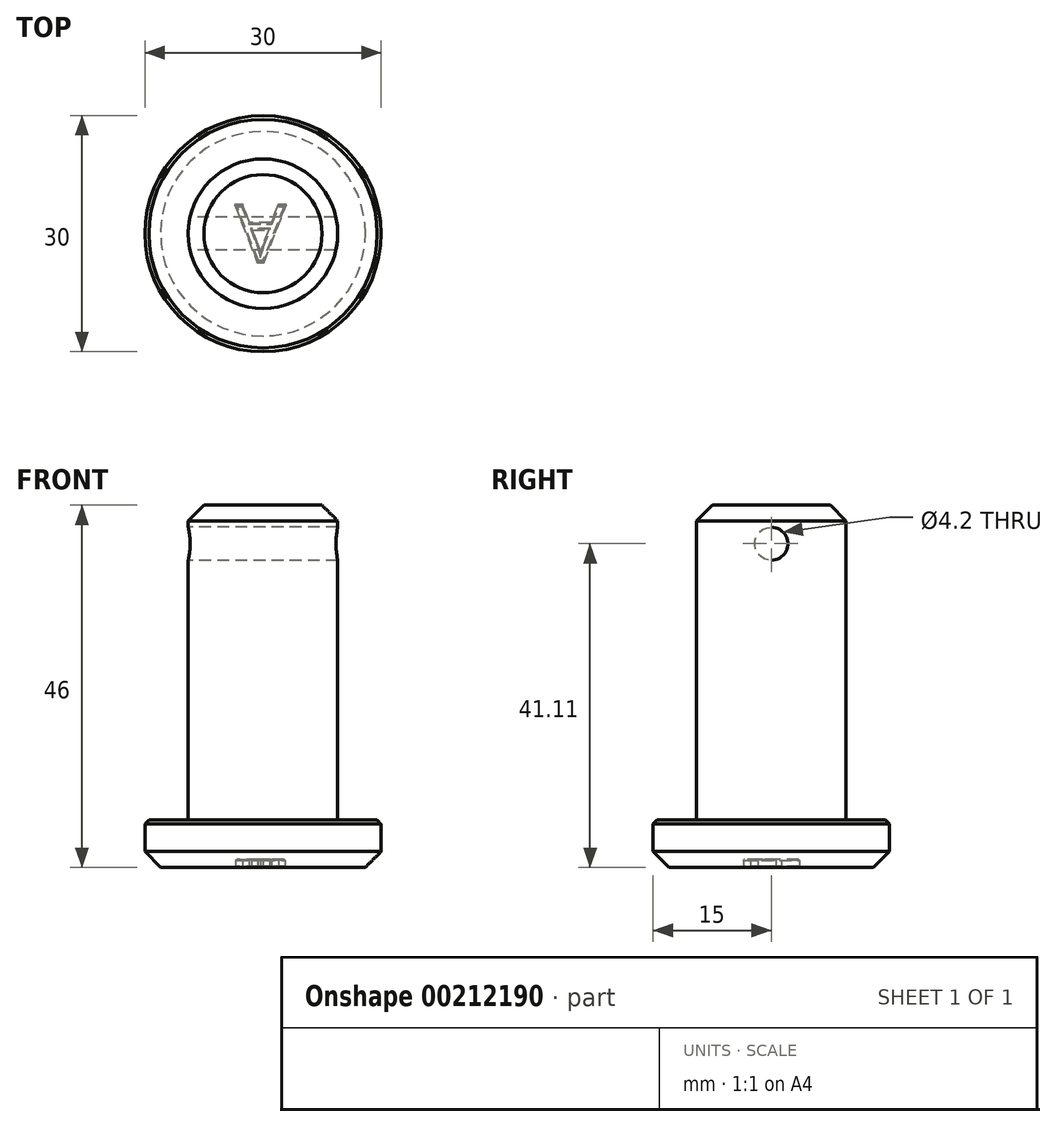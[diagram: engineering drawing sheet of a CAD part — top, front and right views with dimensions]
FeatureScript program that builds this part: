
annotation { "Feature Type Name" : "Feature", "Feature Type Description" : "" }
export const myFeature = defineFeature(function(context is Context, id is Id, definition is map)
    precondition{}
    {
        {
            var Q0;
            Q0=qCreatedBy(makeId("Top.planeOp"),FACE);
            var sketch = newSketch(context, id + "F0", { "sketchPlane" : qUnion([Q0])});
            skCircle(sketch, "E0", {"center": v(0, 0) * mm, "radius": 15 * mm});
            skCircle(sketch, "E1", {"center": v(0, 0) * mm, "radius": 9.5 * mm});
            skSolve(sketch);
        }
        {
            var Q0;
            Q0=makeQuery(id+"F0.imprint","IMPRINT",FACE,{"disambiguationData":[TD([[makeQuery(id+"F0.imprint","IMPRINT",EDGE,{"derivedFrom":sQuery(id+"F0.wireOp",EDGE,"E0")}),1.0]])]});
            extrude(context, id + "F1", {"entities" : qUnion([Q0]), "depth" : 6 * mm});
        }
        {
            var Q0;
            Q0=makeQuery(id+"F0.imprint","IMPRINT",FACE,{"disambiguationData":[TD([[makeQuery(id+"F0.imprint","IMPRINT",EDGE,{"derivedFrom":sQuery(id+"F0.wireOp",EDGE,"E1")}),1.0]])]});
            extrude(context, id + "F2", {"entities" : qUnion([Q0]), "operationType" : NewBodyOperationType.ADD, "depth" : 46 * mm});
        }
        {
            var Q0;
            Q0=qCreatedBy(makeId("Right.planeOp"),FACE);
            var sketch = newSketch(context, id + "F3", { "sketchPlane" : qUnion([Q0])});
            skCircle(sketch, "E2", {"center": v(0, 41.1) * mm, "radius": 2.1 * mm});
            skSolve(sketch);
        }
        {
            var Q0;
            Q0=sQuery(id+"F3.wireOp",VERTEX,"E2.center");
            var Q1;
            Q1=makeQuery(id+"F1.opExtrude","SWEPT_BODY",BODY,{"disambiguationData":[OSD([sQuery(id+"F0.wireOp",EDGE,"E0"),sQuery(id+"F0.wireOp",EDGE,"E1")])]});
            hole(context, id + "F4", {"style" : HoleStyle.SIMPLE, "endStyle" : HoleEndStyle.THROUGH, "oppositeDirection" : true, "standardTappedOrClearance" : lookupTablePath({ "standard" : "ISO", "size" : "4.2", "type" : "Drilled" }), "standardBlindInLast" : lookupTablePath({ "standard" : "ISO", "size" : "4.2", "type" : "Drilled" }), "holeDiameter" : 4.2 * mm, "locations" : qUnion([Q0]), "scope" : qUnion([Q1]), "tappedDepth" : 12 * mm, "tapClearance" : 3});
        }
        {
            var Q0;
            Q0=sQuery(id+"F3.wireOp",VERTEX,"E2.center");
            var Q1;
            Q1=makeQuery(id+"F1.opExtrude","SWEPT_BODY",BODY,{"disambiguationData":[OSD([sQuery(id+"F0.wireOp",EDGE,"E0"),sQuery(id+"F0.wireOp",EDGE,"E1")])]});
            hole(context, id + "F5", {"style" : HoleStyle.SIMPLE, "endStyle" : HoleEndStyle.THROUGH, "standardTappedOrClearance" : lookupTablePath({ "standard" : "ISO", "size" : "4.2", "type" : "Drilled" }), "standardBlindInLast" : lookupTablePath({ "standard" : "ISO", "size" : "4.2", "type" : "Drilled" }), "holeDiameter" : 4.2 * mm, "locations" : qUnion([Q0]), "scope" : qUnion([Q1]), "tappedDepth" : 12 * mm, "tapClearance" : 3});
        }
        {
            var Q0;
            Q0=makeQuery(id+"F2.opExtrude","CAP_EDGE",EDGE,{"disambiguationData":[OSD([sQuery(id+"F0.wireOp",EDGE,"E1")])],"isStart":false});
            var Q1;
            Q1=makeQuery(id+"F1.opExtrude","CAP_EDGE",EDGE,{"disambiguationData":[OSD([sQuery(id+"F0.wireOp",EDGE,"E0")])],"isStart":true});
            chamfer(context, id + "F6", {"entities" : qUnion([Q0, Q1]), "width" : 2 * mm, "tangentPropagation" : true});
        }
        {
            var Q0;
            Q0=makeQuery(id+"F5.hole-0.boolean.opBoolean","INTERSECT",EDGE,{"derivedFrom":[makeQuery(id+"F2.opExtrude","SWEPT_FACE",FACE,{"disambiguationData":[OSD([sQuery(id+"F0.wireOp",EDGE,"E1")])]}),makeQuery(id+"F5.hole-0.opRevolve","SWEPT_FACE",FACE,{"disambiguationData":[OSD([sQuery(id+"F5.hole-0.sketch.wireOp",EDGE,"core_line_2")])]})]});
            var Q1;
            Q1=makeQuery(id+"F4.hole-0.boolean.opBoolean","INTERSECT",EDGE,{"derivedFrom":[makeQuery(id+"F2.opExtrude","SWEPT_FACE",FACE,{"disambiguationData":[OSD([sQuery(id+"F0.wireOp",EDGE,"E1")])]}),makeQuery(id+"F4.hole-0.opRevolve","SWEPT_FACE",FACE,{"disambiguationData":[OSD([sQuery(id+"F4.hole-0.sketch.wireOp",EDGE,"core_line_2")])]})]});
            var Q2;
            Q2=makeQuery(id+"F1.opExtrude","CAP_EDGE",EDGE,{"disambiguationData":[OSD([sQuery(id+"F0.wireOp",EDGE,"E0")])],"isStart":false});
            chamfer(context, id + "F7", {"entities" : qUnion([Q0, Q1, Q2]), "width" : .5 * mm, "tangentPropagation" : true});
        }
        {
            var Q0;
            {var subQ0=sQuery(id+"F0.wireOp",EDGE,"E1");Q0=makeQuery(id+"F2.boolean.opBoolean","MERGE",FACE,{"derivedFrom":[makeQuery(id+"F1.opExtrude","CAP_FACE",FACE,{"disambiguationData":[OSD([sQuery(id+"F0.wireOp",EDGE,"E0"),subQ0])],"isStart":true}),makeQuery(id+"F2.opExtrude","CAP_FACE",FACE,{"disambiguationData":[OSD([subQ0])],"isStart":true})]});}
            var sketch = newSketch(context, id + "F8", { "sketchPlane" : qUnion([Q0])});
            skLineSegment(sketch, "E3.bottom", {"start": v(-3.46, -3.57) * mm, "end": v(3.46, -3.57) * mm, "construction": true});
            skLineSegment(sketch, "E3.top", {"start": v(-3.46, 3.57) * mm, "end": v(3.46, 3.57) * mm, "construction": true});
            skLineSegment(sketch, "E3.left", {"start": v(-3.46, -3.57) * mm, "end": v(-3.46, 3.57) * mm, "construction": true});
            skLineSegment(sketch, "E3.right", {"start": v(3.46, -3.57) * mm, "end": v(3.46, 3.57) * mm, "construction": true});
            skPoint(sketch, "E3.middle", {"position": v(0, 0) * mm});
            skText(sketch, "E4", { "text": "A", "fontName": "OpenSans-Regular.ttf"});
            const initialGuessF8  = {"E4": [-0.00346, -0.00357, 1, 0, 0.00715]};
            skSetInitialGuess(sketch, initialGuessF8);
            skSolve(sketch);
        }
        {
            var Q0;
            Q0=makeQuery(id+"F8.imprint","IMPRINT",FACE,{"disambiguationData":[TD([[makeQuery(id+"F8.imprint","IMPRINT",EDGE,{"derivedFrom":sQuery(id+"F8.wireOp",EDGE,"E4.sketch_text.stroke-0")}),-1.0]])]});
            extrude(context, id + "F9", {"entities" : qUnion([Q0]), "operationType" : NewBodyOperationType.REMOVE, "oppositeDirection" : true, "depth" : 1 * mm});
        }
        {
            var Q0;
            Q0=makeQuery(id+"F9.boolean.opBoolean","COPY",EDGE,{"derivedFrom":makeQuery(id+"F9.opExtrude","CAP_EDGE",EDGE,{"disambiguationData":[OSD([sQuery(id+"F8.wireOp",EDGE,"E4.sketch_text.stroke-1")])],"isStart":true})});
            var Q1;
            Q1=makeQuery(id+"F9.boolean.opBoolean","COPY",EDGE,{"derivedFrom":makeQuery(id+"F9.opExtrude","CAP_EDGE",EDGE,{"disambiguationData":[OSD([sQuery(id+"F8.wireOp",EDGE,"E4.sketch_text.stroke-0")])],"isStart":true})});
            var Q2;
            Q2=makeQuery(id+"F9.boolean.opBoolean","COPY",EDGE,{"derivedFrom":makeQuery(id+"F9.opExtrude","CAP_EDGE",EDGE,{"disambiguationData":[OSD([sQuery(id+"F8.wireOp",EDGE,"E4.sketch_text.stroke-7")])],"isStart":true})});
            var Q3;
            Q3=makeQuery(id+"F9.boolean.opBoolean","COPY",EDGE,{"derivedFrom":makeQuery(id+"F9.opExtrude","CAP_EDGE",EDGE,{"disambiguationData":[OSD([sQuery(id+"F8.wireOp",EDGE,"E4.sketch_text.stroke-6")])],"isStart":true})});
            var Q4;
            Q4=makeQuery(id+"F9.boolean.opBoolean","COPY",EDGE,{"derivedFrom":makeQuery(id+"F9.opExtrude","CAP_EDGE",EDGE,{"disambiguationData":[OSD([sQuery(id+"F8.wireOp",EDGE,"E4.sketch_text.stroke-5")])],"isStart":true})});
            var Q5;
            Q5=makeQuery(id+"F9.boolean.opBoolean","COPY",EDGE,{"derivedFrom":makeQuery(id+"F9.opExtrude","CAP_EDGE",EDGE,{"disambiguationData":[OSD([sQuery(id+"F8.wireOp",EDGE,"E4.sketch_text.stroke-4")])],"isStart":true})});
            var Q6;
            Q6=makeQuery(id+"F9.boolean.opBoolean","COPY",EDGE,{"derivedFrom":makeQuery(id+"F9.opExtrude","CAP_EDGE",EDGE,{"disambiguationData":[OSD([sQuery(id+"F8.wireOp",EDGE,"E4.sketch_text.stroke-3")])],"isStart":true})});
            var Q7;
            Q7=makeQuery(id+"F9.boolean.opBoolean","COPY",EDGE,{"derivedFrom":makeQuery(id+"F9.opExtrude","CAP_EDGE",EDGE,{"disambiguationData":[OSD([sQuery(id+"F8.wireOp",EDGE,"E4.sketch_text.stroke-2")])],"isStart":true})});
            var Q8;
            {var subQ0=sQuery(id+"F0.wireOp",EDGE,"E1");Q8=makeQuery(id+"F9.boolean.opBoolean","SPLIT",FACE,{"disambiguationData":[TD([makeQuery(id+"F9.opExtrude","SWEPT_FACE",FACE,{"disambiguationData":[OSD([sQuery(id+"F8.wireOp",EDGE,"E4.sketch_text.stroke-8")])]})])],"derivedFrom":makeQuery(id+"F2.boolean.opBoolean","MERGE",FACE,{"derivedFrom":[makeQuery(id+"F1.opExtrude","CAP_FACE",FACE,{"disambiguationData":[OSD([sQuery(id+"F0.wireOp",EDGE,"E0"),subQ0])],"isStart":true}),makeQuery(id+"F2.opExtrude","CAP_FACE",FACE,{"disambiguationData":[OSD([subQ0])],"isStart":true})]})});}
            var Q9;
            Q9=makeQuery(id+"F9.boolean.opBoolean","COPY",FACE,{"derivedFrom":makeQuery(id+"F9.opExtrude","CAP_FACE",FACE,{"disambiguationData":[OSD([sQuery(id+"F8.wireOp",EDGE,"E4.sketch_text.stroke-0"),sQuery(id+"F8.wireOp",EDGE,"E4.sketch_text.stroke-1"),sQuery(id+"F8.wireOp",EDGE,"E4.sketch_text.stroke-2"),sQuery(id+"F8.wireOp",EDGE,"E4.sketch_text.stroke-3"),sQuery(id+"F8.wireOp",EDGE,"E4.sketch_text.stroke-4"),sQuery(id+"F8.wireOp",EDGE,"E4.sketch_text.stroke-5"),sQuery(id+"F8.wireOp",EDGE,"E4.sketch_text.stroke-6"),sQuery(id+"F8.wireOp",EDGE,"E4.sketch_text.stroke-7"),sQuery(id+"F8.wireOp",EDGE,"E4.sketch_text.stroke-8"),sQuery(id+"F8.wireOp",EDGE,"E4.sketch_text.stroke-9"),sQuery(id+"F8.wireOp",EDGE,"E4.sketch_text.stroke-10"),sQuery(id+"F8.wireOp",EDGE,"E4.sketch_text.stroke-11"),sQuery(id+"F8.wireOp",EDGE,"E4.sketch_text.stroke-12")])],"isStart":false})});
            chamfer(context, id + "F10", {"entities" : qUnion([Q0, Q1, Q2, Q3, Q4, Q5, Q6, Q7, Q8, Q9]), "width" : 0.1 * mm, "tangentPropagation" : true});
        }
    });
